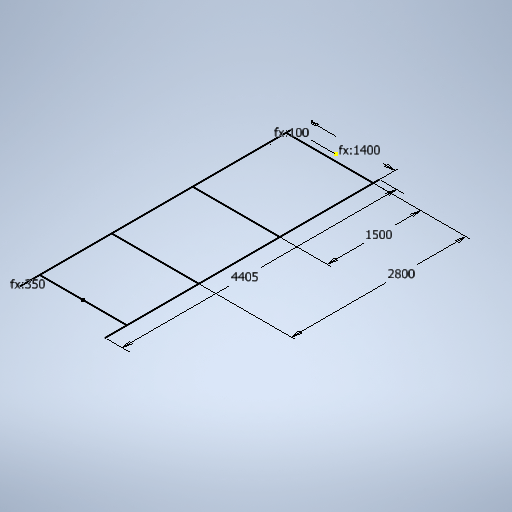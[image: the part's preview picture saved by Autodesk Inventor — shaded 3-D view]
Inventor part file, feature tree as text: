
AUTODESK INVENTOR PART (.ipt)
format: ipt  version: 2025 (Build 290162010, 162A)  size: 265,216 bytes
history: native  units: in
note: dims shown in document units (in); Inventor stores cm internally (conversion verified against a paired STEP export)
features: sketch x1
ambient origin geometry x8: Origin, YZ Plane, XZ Plane, XY Plane, X Axis, Y Axis, Z Axis, Center Point
feature tree (1):
  sketch  "Sketch3"  dims[d7=173.4252in d8=3.937in d9=13.7795in d10=55.1181in d11=59.0551in d12=110.2362in]
